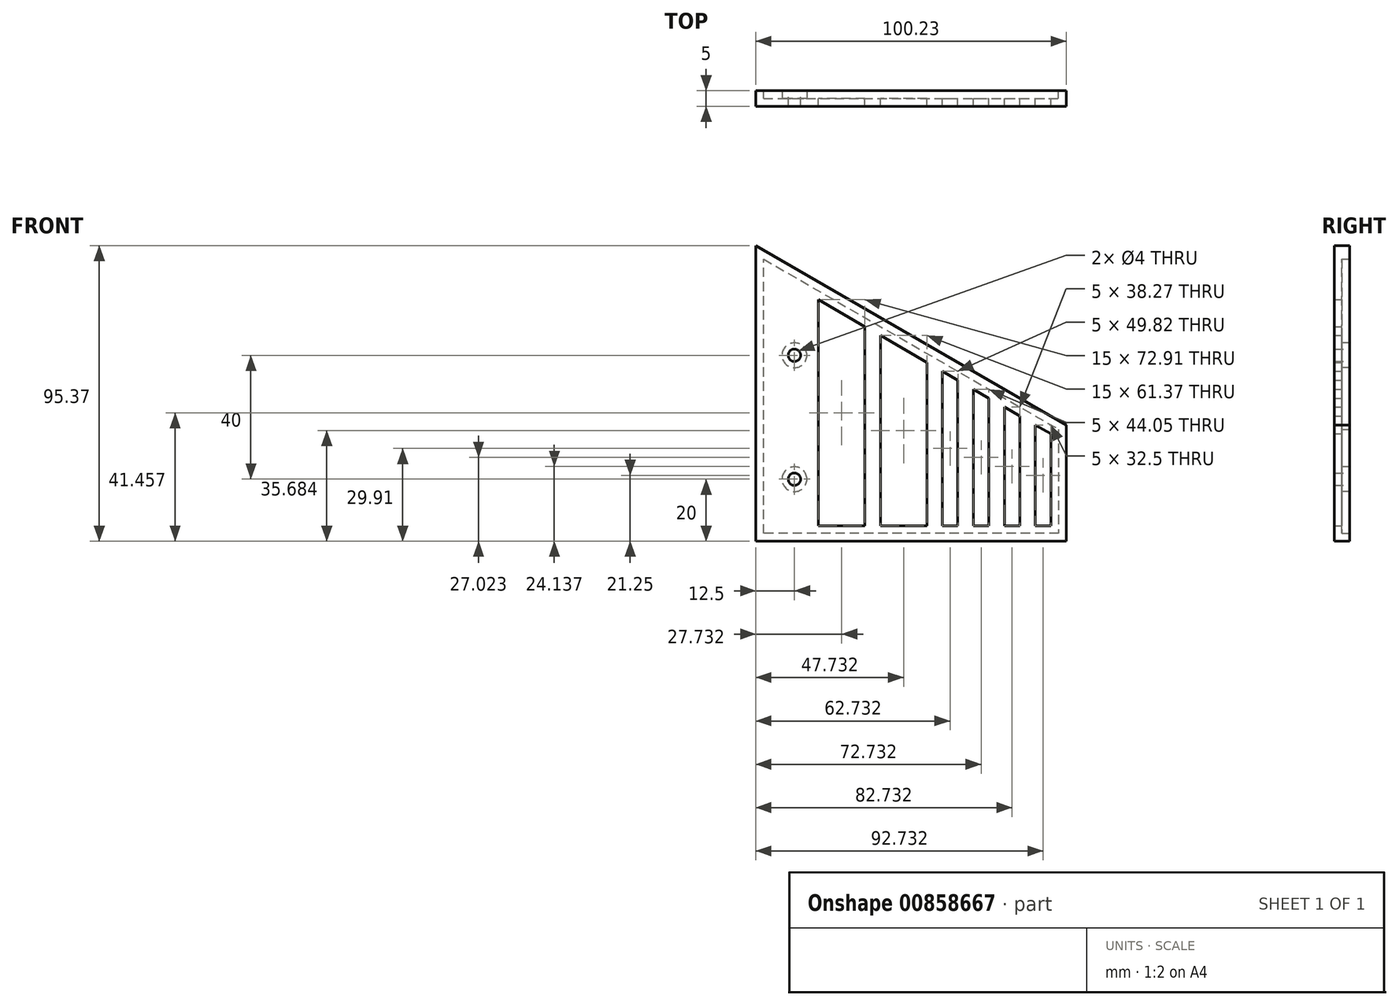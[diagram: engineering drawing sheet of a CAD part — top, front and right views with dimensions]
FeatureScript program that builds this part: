
annotation { "Feature Type Name" : "Feature", "Feature Type Description" : "" }
export const myFeature = defineFeature(function(context is Context, id is Id, definition is map)
    precondition{}
    {
        {
            var Q0;
            Q0=qCreatedBy(makeId("Front.planeOp"),FACE);
            var sketch = newSketch(context, id + "F0", { "sketchPlane" : qUnion([Q0])});
            skLineSegment(sketch, "E0", {"start": v(0, 0) * mm, "end": v(0, 95.37) * mm});
            skLineSegment(sketch, "E1", {"start": v(0, 95.37) * mm, "end": v(100.23, 37.5) * mm});
            skLineSegment(sketch, "E2", {"start": v(100.23, 37.5) * mm, "end": v(100.23, 0) * mm});
            skLineSegment(sketch, "E3", {"start": v(100.23, 0) * mm, "end": v(0, 0) * mm});
            skSolve(sketch);
        }
        {
            var Q0;
            Q0 = qSketchRegion(id + "F0", true);
            extrude(context, id + "F1", {"entities" : qUnion([Q0]), "depth" : 5 * mm, "offsetDistance" : 25 * mm});
        }
        {
            var Q0;
            Q0=makeQuery(id+"F1.opExtrude","CAP_FACE",FACE,{"disambiguationData":[OSD([sQuery(id+"F0.wireOp",EDGE,"E0"),sQuery(id+"F0.wireOp",EDGE,"E1"),sQuery(id+"F0.wireOp",EDGE,"E2"),sQuery(id+"F0.wireOp",EDGE,"E3")])],"isStart":true});
            shell(context, id + "F2", {"entities" : qUnion([Q0]), "thickness" : 2.5 * mm});
        }
        {
            var Q0;
            Q0=makeQuery(id+"F1.opExtrude","CAP_FACE",FACE,{"disambiguationData":[OSD([sQuery(id+"F0.wireOp",EDGE,"E0"),sQuery(id+"F0.wireOp",EDGE,"E1"),sQuery(id+"F0.wireOp",EDGE,"E2"),sQuery(id+"F0.wireOp",EDGE,"E3")])],"isStart":true});
            var sketch = newSketch(context, id + "F3", { "sketchPlane" : qUnion([Q0])});
            skLineSegment(sketch, "E4.0", {"start": v(-95.23, 5) * mm, "end": v(-10.23, 5) * mm, "construction": true});
            skLineSegment(sketch, "E4.1", {"start": v(-95.23, 34.61) * mm, "end": v(-95.23, 5) * mm});
            skLineSegment(sketch, "E4.2", {"start": v(-10.23, 83.69) * mm, "end": v(-95.23, 34.61) * mm, "construction": true});
            skLineSegment(sketch, "E4.3", {"start": v(-10.23, 5) * mm, "end": v(-10.23, 83.69) * mm, "construction": true});
            skLineSegment(sketch, "E5", {"start": v(-90.23, 5) * mm, "end": v(-90.23, 37.5) * mm});
            skLineSegment(sketch, "E6", {"start": v(-85.23, 5) * mm, "end": v(-85.23, 40.39) * mm});
            skLineSegment(sketch, "E7", {"start": v(-80.23, 5) * mm, "end": v(-80.23, 43.27) * mm});
            skLineSegment(sketch, "E8", {"start": v(-75.23, 5) * mm, "end": v(-75.23, 46.16) * mm});
            skLineSegment(sketch, "E9", {"start": v(-70.23, 5) * mm, "end": v(-70.23, 49.05) * mm});
            skLineSegment(sketch, "E10", {"start": v(-65.23, 5) * mm, "end": v(-65.23, 51.93) * mm});
            skLineSegment(sketch, "E11", {"start": v(-60.23, 5) * mm, "end": v(-60.23, 54.82) * mm});
            skLineSegment(sketch, "E12", {"start": v(-55.23, 5) * mm, "end": v(-55.23, 57.7) * mm});
            skLineSegment(sketch, "E13", {"start": v(-50.23, 5) * mm, "end": v(-50.23, 60.6) * mm});
            skLineSegment(sketch, "E14", {"start": v(-45.23, 5) * mm, "end": v(-45.23, 63.48) * mm});
            skLineSegment(sketch, "E15", {"start": v(-40.23, 5) * mm, "end": v(-40.23, 66.37) * mm});
            skLineSegment(sketch, "E16", {"start": v(-35.23, 69.25) * mm, "end": v(-35.23, 5) * mm});
            skLineSegment(sketch, "E17", {"start": v(-30.23, 5) * mm, "end": v(-30.23, 72.14) * mm});
            skLineSegment(sketch, "E18", {"start": v(-25.23, 5) * mm, "end": v(-25.23, 75.03) * mm});
            skLineSegment(sketch, "E19", {"start": v(-20.23, 5) * mm, "end": v(-20.23, 77.91) * mm});
            skLineSegment(sketch, "E20", {"start": v(-15.23, 5) * mm, "end": v(-15.23, 80.8) * mm});
            skLineSegment(sketch, "E21", {"start": v(-95.23, 34.61) * mm, "end": v(-90.23, 37.5) * mm});
            skLineSegment(sketch, "E22", {"start": v(-85.23, 40.39) * mm, "end": v(-80.23, 43.27) * mm});
            skLineSegment(sketch, "E23", {"start": v(-75.23, 46.16) * mm, "end": v(-70.23, 49.05) * mm});
            skLineSegment(sketch, "E24", {"start": v(-65.23, 51.93) * mm, "end": v(-60.23, 54.82) * mm});
            skLineSegment(sketch, "E25", {"start": v(-55.23, 57.7) * mm, "end": v(-50.23, 60.6) * mm});
            skLineSegment(sketch, "E26", {"start": v(-45.23, 63.48) * mm, "end": v(-40.23, 66.37) * mm});
            skLineSegment(sketch, "E27", {"start": v(-35.23, 69.25) * mm, "end": v(-30.23, 72.14) * mm});
            skLineSegment(sketch, "E28", {"start": v(-25.23, 75.03) * mm, "end": v(-20.23, 77.91) * mm});
            skLineSegment(sketch, "E29", {"start": v(-15.23, 80.8) * mm, "end": v(-10.23, 83.69) * mm});
            skLineSegment(sketch, "E30", {"start": v(-10.23, 5) * mm, "end": v(-15.23, 5) * mm});
            skLineSegment(sketch, "E31", {"start": v(-20.23, 5) * mm, "end": v(-25.23, 5) * mm});
            skLineSegment(sketch, "E32", {"start": v(-30.23, 5) * mm, "end": v(-35.23, 5) * mm});
            skLineSegment(sketch, "E33", {"start": v(-40.23, 5) * mm, "end": v(-45.23, 5) * mm});
            skLineSegment(sketch, "E34", {"start": v(-50.23, 5) * mm, "end": v(-55.23, 5) * mm});
            skLineSegment(sketch, "E35", {"start": v(-60.23, 5) * mm, "end": v(-65.23, 5) * mm});
            skLineSegment(sketch, "E36", {"start": v(-70.23, 5) * mm, "end": v(-75.23, 5) * mm});
            skLineSegment(sketch, "E37", {"start": v(-80.23, 5) * mm, "end": v(-85.23, 5) * mm});
            skLineSegment(sketch, "E38", {"start": v(-90.23, 5) * mm, "end": v(-95.23, 5) * mm});
            skLineSegment(sketch, "E39", {"start": v(-30.23, 72.14) * mm, "end": v(-25.23, 75.03) * mm});
            skLineSegment(sketch, "E40", {"start": v(-30.23, 5) * mm, "end": v(-25.23, 5) * mm});
            skLineSegment(sketch, "E41", {"start": v(-45.23, 63.48) * mm, "end": v(-50.23, 60.6) * mm});
            skLineSegment(sketch, "E42", {"start": v(-50.23, 5) * mm, "end": v(-45.23, 5) * mm});
            skSolve(sketch);
        }
        {
            var Q0;
            Q0 = qSketchRegion(id + "F3", true);
            extrude(context, id + "F4", {"entities" : qUnion([Q0]), "operationType" : NewBodyOperationType.REMOVE, "endBound" : BoundingType.THROUGH_ALL, "oppositeDirection" : true, "depth" : 25 * mm, "offsetDistance" : 25 * mm});
        }
        {
            var Q0;
            Q0=makeQuery(id+"F1.opExtrude","CAP_FACE",FACE,{"disambiguationData":[OSD([sQuery(id+"F0.wireOp",EDGE,"E0"),sQuery(id+"F0.wireOp",EDGE,"E1"),sQuery(id+"F0.wireOp",EDGE,"E2"),sQuery(id+"F0.wireOp",EDGE,"E3")])],"isStart":true});
            var sketch = newSketch(context, id + "F5", { "sketchPlane" : qUnion([Q0])});
            skCircle(sketch, "E43", {"center": v(-12.5, 60) * mm, "radius": 2 * mm});
            skCircle(sketch, "E44", {"center": v(-12.5, 20) * mm, "radius": 2 * mm});
            skSolve(sketch);
        }
        {
            var Q0;
            Q0 = qSketchRegion(id + "F5", true);
            extrude(context, id + "F6", {"entities" : qUnion([Q0]), "operationType" : NewBodyOperationType.REMOVE, "endBound" : BoundingType.THROUGH_ALL, "oppositeDirection" : true, "depth" : 25 * mm, "offsetDistance" : 25 * mm});
        }
        {
            var Q0;
            Q0=makeQuery(id+"F2.opShell","OFFSET_FACE",FACE,{"disambiguationData":[OSD([sQuery(id+"F0.wireOp",EDGE,"E0"),sQuery(id+"F0.wireOp",EDGE,"E1"),sQuery(id+"F0.wireOp",EDGE,"E2"),sQuery(id+"F0.wireOp",EDGE,"E3")])]});
            var sketch = newSketch(context, id + "F7", { "sketchPlane" : qUnion([Q0])});
            skCircle(sketch, "E45", {"center": v(-12.5, 60) * mm, "radius": 4 * mm});
            skCircle(sketch, "E46", {"center": v(-12.5, 20) * mm, "radius": 4 * mm});
            skCircle(sketch, "E47", {"center": v(-12.5, 60) * mm, "radius": 2 * mm});
            skCircle(sketch, "E48", {"center": v(-12.5, 20) * mm, "radius": 2 * mm});
            skSolve(sketch);
        }
        {
            var Q0;
            Q0 = qSketchRegion(id + "F7", true);
            var Q1;
            Q1=makeQuery(id+"F1.opExtrude","CAP_FACE",FACE,{"disambiguationData":[OSD([sQuery(id+"F0.wireOp",EDGE,"E0"),sQuery(id+"F0.wireOp",EDGE,"E1"),sQuery(id+"F0.wireOp",EDGE,"E2"),sQuery(id+"F0.wireOp",EDGE,"E3")])],"isStart":true});
            extrude(context, id + "F8", {"entities" : qUnion([Q0]), "operationType" : NewBodyOperationType.ADD, "endBound" : BoundingType.UP_TO_SURFACE, "depth" : 25 * mm, "endBoundEntityFace" : qUnion([Q1]), "offsetDistance" : 25 * mm});
        }
    });
